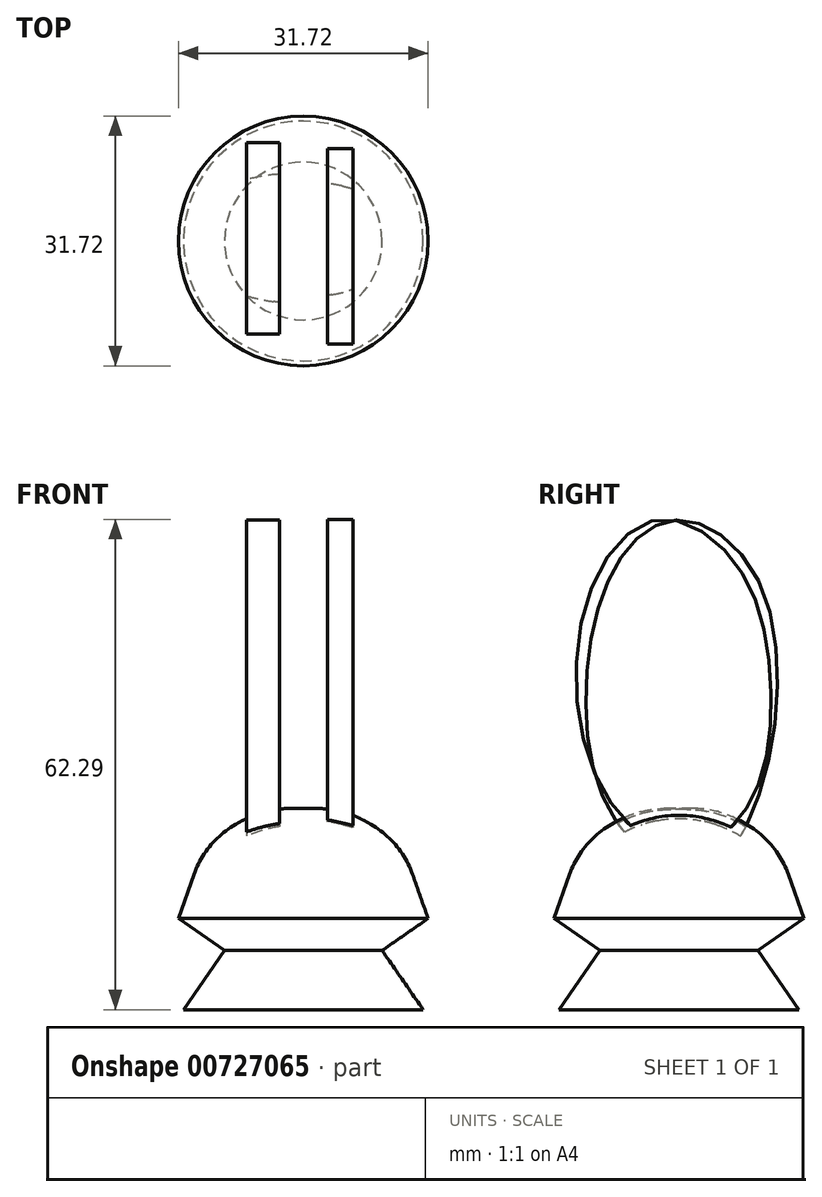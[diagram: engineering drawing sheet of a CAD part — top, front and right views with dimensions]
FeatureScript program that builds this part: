
annotation { "Feature Type Name" : "Feature", "Feature Type Description" : "" }
export const myFeature = defineFeature(function(context is Context, id is Id, definition is map)
    precondition{}
    {
        {
            var Q0;
            Q0=qCreatedBy(makeId("Front.planeOp"),FACE);
            var sketch = newSketch(context, id + "F0", { "sketchPlane" : qUnion([Q0])});
            skLineSegment(sketch, "E0", {"start": v(0, 0) * mm, "end": v(-15.23, 0) * mm});
            skLineSegment(sketch, "E1", {"start": v(-15.23, 0) * mm, "end": v(-10.02, 7.51) * mm});
            skLineSegment(sketch, "E2", {"start": v(-10.02, 7.51) * mm, "end": v(-15.86, 11.57) * mm});
            skLineSegment(sketch, "E3", {"start": v(-15.86, 11.57) * mm, "end": v(-12.42, 21.34) * mm});
            skLineSegment(sketch, "E4", {"start": v(-12.42, 21.34) * mm, "end": v(-5, 25.55) * mm});
            skLineSegment(sketch, "E5", {"start": v(-5, 25.55) * mm, "end": v(0, 25.55) * mm});
            skLineSegment(sketch, "E6", {"start": v(0, 25.55) * mm, "end": v(0, 0) * mm});
            skSolve(sketch);
        }
        {
            var Q0;
            Q0 = qSketchRegion(id + "F0", true);
            var Q1;
            Q1=sQuery(id+"F0.wireOp",EDGE,"E6");
            revolve(context, id + "F1", {"surfaceOperationType" : NewSurfaceOperationType.NEW, "entities" : qUnion([Q0]), "axis" : qUnion([Q1]), "revolveType" : RevolveType.FULL});
        }
        {
            var Q0;
            Q0=makeQuery(id+"F1.opRevolve","SWEPT_FACE",FACE,{"disambiguationData":[OSD([sQuery(id+"F0.wireOp",EDGE,"E4")])]});
            fillet(context, id + "F2", {"entities" : qUnion([Q0]), "radius" : 11.8 * mm, "tangentPropagation" : true, "allowEdgeOverflow" : false});
        }
        {
            var Q0;
            Q0=qCreatedBy(makeId("Right.planeOp"),FACE);
            cPlane(context, id + "F3", {"entities" : qUnion([Q0]), "cplaneType" : CPlaneType.OFFSET, "offset" : 4.7 * mm, "width" : 150 * mm, "height" : 150 * mm});
        }
        {
            var Q0;
            Q0=qCreatedBy(id+"F3.planeOp",FACE);
            var sketch = newSketch(context, id + "F4", { "sketchPlane" : qUnion([Q0])});
            skFitSpline(sketch, "E7", {"points": [v(-2.8, 62.22) * mm, v(-11.62, 52.2) * mm, v(-11.02, 30.76) * mm, v(-2.6, 21.14) * mm, v(5, 21.94) * mm, v(10.42, 29.56) * mm, v(11.42, 44.38) * mm, v(6.81, 57.2) * mm, v(-2.8, 62.22) * mm]});
            skSolve(sketch);
        }
        {
            var Q0;
            Q0=makeQuery(id+"F4.imprint","IMPRINT",FACE,{"disambiguationData":[TD([[makeQuery(id+"F4.imprint","IMPRINT",EDGE,{"derivedFrom":sQuery(id+"F4.wireOp",EDGE,"E7")}),1.0]])]});
            extrude(context, id + "F5", {"entities" : qUnion([Q0]), "operationType" : NewBodyOperationType.ADD, "endBound" : BoundingType.SYMMETRIC, "depth" : 3.2 * mm, "offsetDistance" : 25 * mm});
        }
        {
            var Q0;
            Q0=qCreatedBy(makeId("Right.planeOp"),FACE);
            cPlane(context, id + "F6", {"entities" : qUnion([Q0]), "cplaneType" : CPlaneType.OFFSET, "offset" : 5.1 * mm, "oppositeDirection" : true, "width" : 150 * mm, "height" : 150 * mm});
        }
        {
            var Q0;
            Q0=qCreatedBy(id+"F6.planeOp",FACE);
            var sketch = newSketch(context, id + "F7", { "sketchPlane" : qUnion([Q0])});
            skFitSpline(sketch, "E8", {"points": [v(0.2, 62.22) * mm, v(10.22, 54.2) * mm, v(10.82, 29.36) * mm, v(3, 18.13) * mm, v(-7.41, 23.14) * mm, v(-11.82, 40.18) * mm, v(-7.61, 57) * mm, v(0.2, 62.22) * mm]});
            skSolve(sketch);
        }
        {
            var Q0;
            Q0=makeQuery(id+"F7.imprint","IMPRINT",FACE,{"disambiguationData":[TD([[makeQuery(id+"F7.imprint","IMPRINT",EDGE,{"derivedFrom":sQuery(id+"F7.wireOp",EDGE,"E8")}),-1.0]])]});
            extrude(context, id + "F8", {"entities" : qUnion([Q0]), "operationType" : NewBodyOperationType.ADD, "endBound" : BoundingType.SYMMETRIC, "depth" : 4.2 * mm, "offsetDistance" : 25 * mm});
        }
    });
